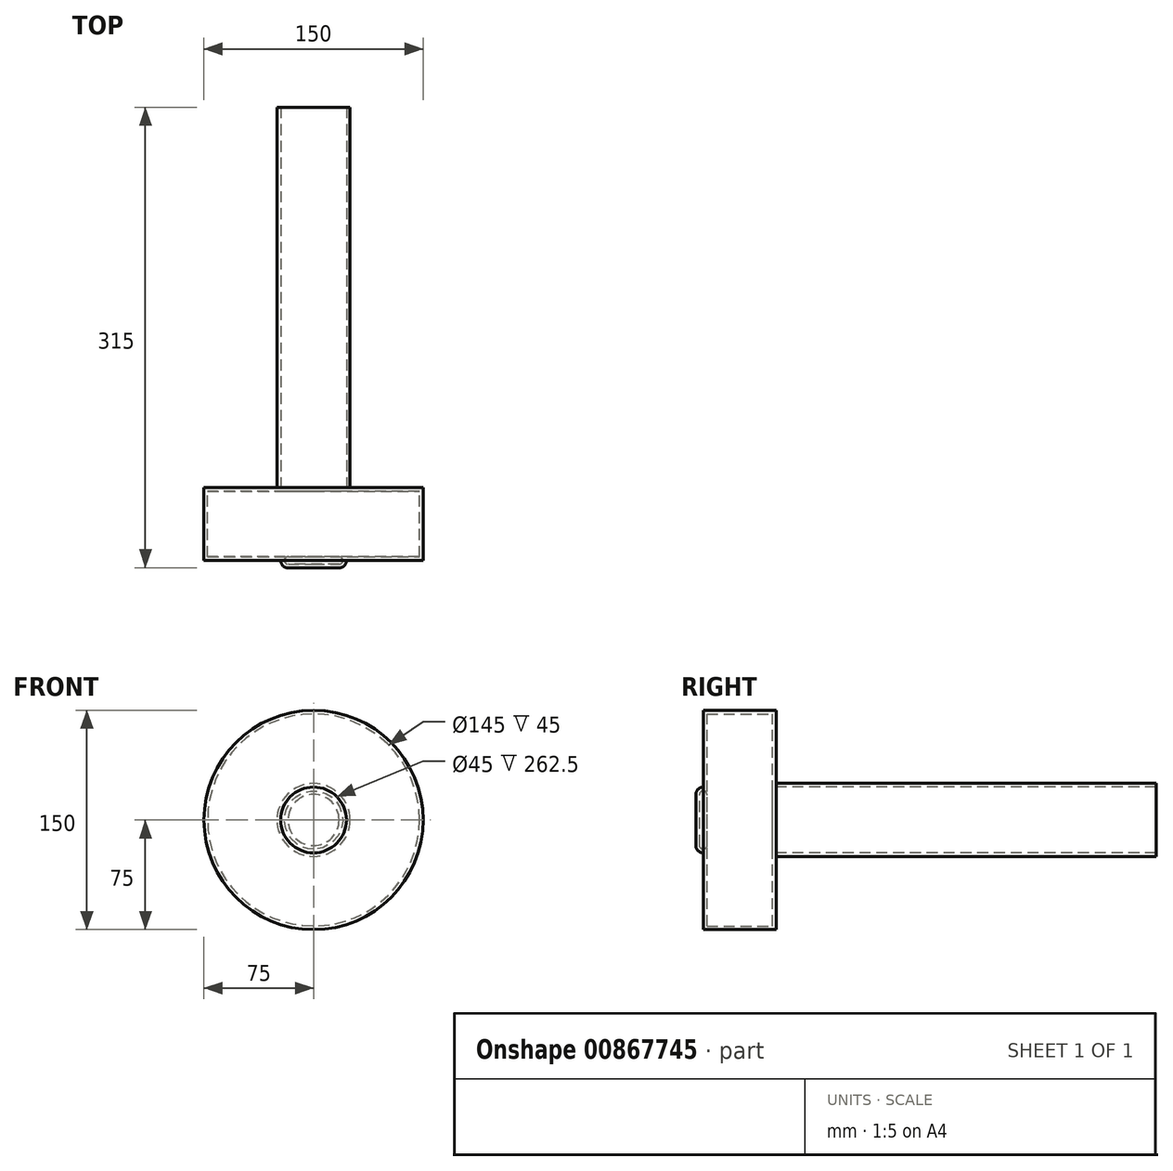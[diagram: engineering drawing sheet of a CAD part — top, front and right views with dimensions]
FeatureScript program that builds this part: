
annotation { "Feature Type Name" : "Feature", "Feature Type Description" : "" }
export const myFeature = defineFeature(function(context is Context, id is Id, definition is map)
    precondition{}
    {
        {
            var Q0;
            Q0=qCreatedBy(makeId("Front.planeOp"),FACE);
            var sketch = newSketch(context, id + "F0", { "sketchPlane" : qUnion([Q0])});
            skCircle(sketch, "E0", {"center": v(0, 0) * mm, "radius": 75 * mm});
            skSolve(sketch);
        }
        {
            var Q0;
            Q0=makeQuery(id+"F0.imprint","IMPRINT",FACE,{"disambiguationData":[TD([[makeQuery(id+"F0.imprint","IMPRINT",EDGE,{"derivedFrom":sQuery(id+"F0.wireOp",EDGE,"E0")}),1.0]])]});
            extrude(context, id + "F1", {"entities" : qUnion([Q0]), "depth" : 50 * mm, "offsetDistance" : 25 * mm});
        }
        {
            var Q0;
            Q0=makeQuery(id+"F1.opExtrude","CAP_FACE",FACE,{"disambiguationData":[OSD([sQuery(id+"F0.wireOp",EDGE,"E0")])],"isStart":true});
            var sketch = newSketch(context, id + "F2", { "sketchPlane" : qUnion([Q0])});
            skCircle(sketch, "E1", {"center": v(0, 0) * mm, "radius": 25 * mm});
            skSolve(sketch);
        }
        {
            var Q0;
            Q0=makeQuery(id+"F2.imprint","IMPRINT",FACE,{"disambiguationData":[TD([[makeQuery(id+"F2.imprint","IMPRINT",EDGE,{"derivedFrom":sQuery(id+"F2.wireOp",EDGE,"E1")}),1.0]])]});
            extrude(context, id + "F3", {"entities" : qUnion([Q0]), "operationType" : NewBodyOperationType.ADD, "depth" : 260 * mm, "offsetDistance" : 25 * mm});
        }
        {
            var Q0;
            Q0=makeQuery(id+"F1.opExtrude","CAP_FACE",FACE,{"disambiguationData":[OSD([sQuery(id+"F0.wireOp",EDGE,"E0")])],"isStart":false});
            var sketch = newSketch(context, id + "F4", { "sketchPlane" : qUnion([Q0])});
            skCircle(sketch, "E2", {"center": v(0, 0) * mm, "radius": 22.5 * mm});
            skSolve(sketch);
        }
        {
            var Q0;
            Q0=makeQuery(id+"F4.imprint","IMPRINT",FACE,{"disambiguationData":[TD([[makeQuery(id+"F4.imprint","IMPRINT",EDGE,{"derivedFrom":sQuery(id+"F4.wireOp",EDGE,"E2")}),1.0]])]});
            extrude(context, id + "F5", {"entities" : qUnion([Q0]), "operationType" : NewBodyOperationType.ADD, "depth" : 5 * mm, "offsetDistance" : 25 * mm});
        }
        {
            var Q0;
            Q0=makeQuery(id+"F5.opExtrude","CAP_EDGE",EDGE,{"disambiguationData":[OSD([sQuery(id+"F4.wireOp",EDGE,"E2")])],"isStart":false});
            fillet(context, id + "F6", {"entities" : qUnion([Q0]), "radius" : 5 * mm, "tangentPropagation" : true, "allowEdgeOverflow" : false});
        }
        {
            var Q0;
            Q0=makeQuery(id+"F3.opExtrude","CAP_FACE",FACE,{"disambiguationData":[OSD([sQuery(id+"F2.wireOp",EDGE,"E1")])],"isStart":false});
            shell(context, id + "F7", {"entities" : qUnion([Q0]), "thickness" : 2.5 * mm});
        }
        {
            var Q0;
            Q0=makeQuery(id+"F1.opExtrude","SWEPT_BODY",BODY,{"disambiguationData":[OSD([sQuery(id+"F0.wireOp",EDGE,"E0")])]});
            transform(context, id + "F8", {"entities" : qUnion([Q0]), "transformType" : TransformType.TRANSLATION_3D, "dx" : 0 * mm, "dy" : 0 * mm, "dz" : 0 * mm, "makeCopy" : false});
        }
    });
